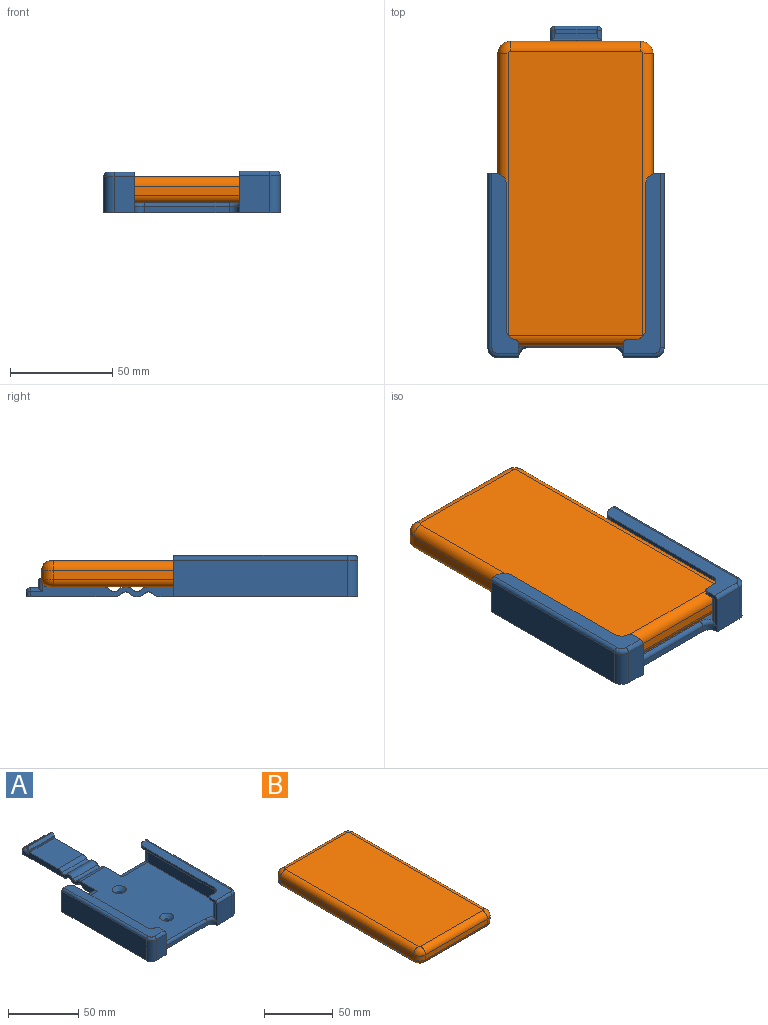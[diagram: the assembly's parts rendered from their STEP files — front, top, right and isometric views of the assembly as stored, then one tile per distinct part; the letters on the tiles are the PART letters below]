
ASSEMBLY  parts=2 mates=1
PART A: 85 faces, bbox 87.1x162.5x20.6 mm
  f0: plane 98.24x76.2mm, normal (0,0,1), area 6276mm2, adj f10,f11,f14,f16,f38,f39,f41,f42
  f1: plane 96.64x86.2mm, normal (0,0,-1), area 7642.9mm2, adj f6,f9,f13,f15,f18,f28,f29,f30
  f2: plane 4x2mm, normal (0,1,0), area 7.1mm2, adj f19,f20,f37,f84
  f3: plane 71x2mm, normal (-1,0,0), area 142mm2, adj f23,f24,f27,f83
  f4: plane 71.07x2mm, normal (1,0,0), area 142.1mm2, adj f19,f20,f22,f84
  f5: plane 4x2mm, normal (0,1,0), area 7.1mm2, adj f23,f24,f34,f83
  f6: plane 41.2x3mm, normal (0,-1,0), area 123.6mm2, adj f1,f28,f29,f48
  f7: plane 28.41x25mm, normal (0,0,1), area 710.2mm2, adj f38,f39,f44,f70
  f8: plane 43x25mm, normal (0,0,-1), area 1073.3mm2, adj f38,f39,f51,f69,f75,f78
  f9: plane 85x18.5mm, normal (1,0,0), area 1572.5mm2, adj f1,f31,f34,f43
  f10: plane 80x13.5mm, normal (-1,0,0), area 1080mm2, adj f0,f11,f23,f43
  f11: plane 13.5x12mm, normal (0,1,0), area 162mm2, adj f0,f10,f23,f72
  f12: plane 17.55x7.05mm, normal (-1,0,0), area 42.9mm2, adj f13,f23,f24,f26,f32,f49,f72
  f13: plane 18.5x15mm, normal (0,-1,0), area 277.5mm2, adj f1,f12,f29,f31,f32
  f14: plane 80x13mm, normal (1,0,0), area 1040mm2, adj f0,f16,f20,f40
  f15: plane 85x18mm, normal (-1,0,0), area 1530mm2, adj f1,f30,f37,f40
  f16: plane 13x7mm, normal (0,1,0), area 91mm2, adj f0,f14,f20,f71
  f17: plane 17.05x7.05mm, normal (1,0,0), area 41.9mm2, adj f18,f19,f20,f21,f35,f47,f71
  f18: plane 18x10mm, normal (0,-1,0), area 180mm2, adj f1,f17,f28,f30,f35
  f19: plane 88x13mm, normal (0,0,1), area 654.9mm2, adj f2,f4,f17,f21,f22,f35,f36,f37
  f20: plane 88x15mm, normal (0,0,-1), area 370.1mm2, adj f2,f4,f14,f16,f17,f21,f22,f40
  f21: cylinder r=2mm len=2mm, axis (0,0,-1), area 5.7mm2, adj f17,f19,f20,f22
  f22: cylinder r=5mm len=4.95mm, axis (0,0,-1), area 14.3mm2, adj f4,f19,f20,f21
  f23: plane 88x20mm, normal (0,0,-1), area 390.4mm2, adj f3,f5,f10,f11,f12,f25,f26,f27
  f24: plane 88x18mm, normal (0,0,1), area 690.2mm2, adj f3,f5,f12,f25,f26,f27,f32,f33
  f25: plane 4x2mm, normal (0,1,0), area 8mm2, adj f23,f24,f26,f27
  f26: cylinder r=2mm len=2mm, axis (0,0,1), area 6.3mm2, adj f12,f23,f24,f25
  f27: cylinder r=5mm len=5mm, axis (0,0,-1), area 15.7mm2, adj f3,f23,f24,f25
  f28: cylinder r=5mm len=5mm, axis (0,0,1), area 23.6mm2, adj f1,f6,f18,f47
  f29: cylinder r=5mm len=5mm, axis (0,0,-1), area 23.6mm2, adj f1,f6,f13,f49
  f30: cylinder r=5mm len=18mm, axis (0,0,-1), area 141.4mm2, adj f1,f15,f18,f36
  f31: cylinder r=5mm len=18.5mm, axis (0,0,-1), area 145.3mm2, adj f1,f9,f13,f33
  f32: cylinder r=2mm len=15mm, axis (-1,0,0), area 47.1mm2, adj f12,f13,f24,f33
  f33: torus R=3mm, axis (0,0,1), area 21.1mm2, adj f24,f31,f32,f34
  f34: cylinder r=2mm len=85mm, axis (0,-1,0), area 267mm2, adj f5,f9,f24,f33
  f35: cylinder r=2mm len=10mm, axis (1,0,0), area 31.4mm2, adj f17,f18,f19,f36
  f36: torus R=3mm, axis (0,0,1), area 21.1mm2, adj f19,f30,f35,f37
  f37: cylinder r=2mm len=85mm, axis (0,-1,0), area 267mm2, adj f2,f15,f19,f36
  f38: plane 75x8mm, normal (1,0,0), area 294.1mm2, adj f0,f1,f7,f8,f42,f44,f46,f61
  f39: plane 75x8mm, normal (-1,0,0), area 294.1mm2, adj f0,f1,f7,f8,f41,f44,f46,f61
  f40: cylinder r=5mm len=18mm, axis (0,0,-1), area 116.4mm2, adj f14,f15,f20,f41
  f41: cylinder r=5mm len=30.6mm, axis (1,0,0), area 215.3mm2, adj f0,f1,f39,f40
  f42: cylinder r=5mm len=30.6mm, axis (1,0,0), area 215.3mm2, adj f0,f1,f38,f43
  f43: cylinder r=5mm len=18.5mm, axis (0,0,-1), area 120.3mm2, adj f9,f10,f23,f42
  f44: plane 25x2mm, normal (0,-1,0), area 50mm2, adj f7,f38,f39,f46
  f45: plane 21x3.5mm, normal (0,1,0), area 73.5mm2, adj f50,f73,f74,f82
  f46: plane 25.04x2.04mm, normal (0,-0.71,0.71), area 70.5mm2, adj f38,f39,f44,f73,f74,f82
  f47: torus R=7mm, axis (0,0,1), area 20.9mm2, adj f0,f17,f28,f48,f71
  f48: cylinder r=2mm len=41.2mm, axis (-1,0,0), area 129.4mm2, adj f0,f6,f47,f49
  f49: torus R=7mm, axis (0,0,1), area 20.9mm2, adj f0,f12,f29,f48,f72
  f50: plane 21x4mm, normal (0,0,1), area 48.4mm2, adj f45,f52,f53,f54,f76,f79,f81
  f51: plane 21x2.5mm, normal (0,1,0), area 52.5mm2, adj f8,f75,f78,f79
  f52: plane 2x0.7mm, normal (1,0,0), area 1.4mm2, adj f50,f53,f55,f56,f79
  f53: plane 20x0.7mm, normal (0,1,0), area 14mm2, adj f50,f52,f54,f56
  f54: plane 2x0.7mm, normal (-1,0,0), area 1.4mm2, adj f50,f53,f55,f56,f79
  f55: plane 20x0.69mm, normal (0,-1,0), area 13.8mm2, adj f52,f54,f56,f79
  f56: plane 20x2mm, normal (0,0,1), area 40mm2, adj f52,f53,f54,f55
  f57: cylinder r=2mm len=4mm, axis (0,0,1), area 25.1mm2, adj f1,f58
  f58: cone r=2mm half-angle=45deg, axis (0,0,1), area 93.3mm2, adj f0,f57
  f59: cylinder r=2mm len=4mm, axis (0,0,1), area 25.1mm2, adj f1,f60
  f60: cone r=2mm half-angle=45deg, axis (0,0,1), area 93.3mm2, adj f0,f59
  f61: cylinder r=2.5mm len=25mm, axis (1,0,0), area 105.1mm2, adj f38,f39,f66,f69
  f62: cylinder r=2.5mm len=25mm, axis (1,0,0), area 105.1mm2, adj f38,f39,f65,f66
  f63: cylinder r=2.5mm len=25mm, axis (1,0,0), area 105.1mm2, adj f38,f39,f68,f70
  f64: cylinder r=2.5mm len=25mm, axis (1,0,0), area 105.1mm2, adj f38,f39,f67,f68
  f65: cylinder r=5mm len=25mm, axis (1,0,0), area 105.1mm2, adj f1,f38,f39,f62
  f66: cylinder r=5mm len=25mm, axis (1,0,0), area 210.3mm2, adj f38,f39,f61,f62
  f67: cylinder r=5mm len=25mm, axis (1,0,0), area 105.1mm2, adj f0,f38,f39,f64
  f68: cylinder r=5mm len=25mm, axis (1,0,0), area 210.3mm2, adj f38,f39,f63,f64
  f69: cylinder r=5mm len=25mm, axis (1,0,0), area 105.1mm2, adj f8,f38,f39,f61
  f70: cylinder r=5mm len=25mm, axis (1,0,0), area 105.1mm2, adj f7,f38,f39,f63
  f71: cylinder r=3mm len=13.82mm, axis (0,0,1), area 61.9mm2, adj f0,f16,f17,f20,f47
  f72: cylinder r=3mm len=14.32mm, axis (0,0,-1), area 64.3mm2, adj f0,f11,f12,f23,f49
  f73: cylinder r=1mm len=24.46mm, axis (-1,0,0), area 36.1mm2, adj f45,f46,f74,f82
  f74: cylinder r=2mm len=6.5mm, axis (0,0,-1), area 15.1mm2, adj f38,f45,f46,f73,f76
  f75: cylinder r=2mm len=2.5mm, axis (0,0,-1), area 7.9mm2, adj f8,f38,f51,f77
  f76: cylinder r=2mm len=6mm, axis (0,1,0), area 14.8mm2, adj f38,f50,f74,f77
  f77: sphere r=2mm, area 6.3mm2, adj f75,f76,f79
  f78: cylinder r=2mm len=2.5mm, axis (0,0,1), area 7.9mm2, adj f8,f39,f51,f80
  f79: cylinder r=2mm len=21mm, axis (-1,0,0), area 61.5mm2, adj f50,f51,f52,f54,f55,f77,f80
  f80: sphere r=2mm, area 6.3mm2, adj f78,f79,f81
  f81: cylinder r=2mm len=6mm, axis (0,-1,0), area 14.8mm2, adj f39,f50,f80,f82
  f82: cylinder r=2mm len=6.5mm, axis (0,0,1), area 15.1mm2, adj f39,f45,f46,f73,f81
  f83: cylinder r=5mm len=5mm, axis (0,0,-1), area 15.7mm2, adj f3,f5,f23,f24
  f84: cylinder r=5mm len=5mm, axis (0,0,1), area 15.7mm2, adj f2,f4,f19,f20
PART B: 26 faces, bbox 75.8x148.9x12.8 mm
  f0: plane 63.8x4.3mm, normal (0,-1,0), area 274.3mm2, adj f6,f9,f17,f25
  f1: plane 136.86x4.3mm, normal (1,0,0), area 588.5mm2, adj f6,f7,f13,f21
  f2: plane 63.8x4.3mm, normal (0,1,0), area 274.3mm2, adj f7,f8,f10,f18
  f3: plane 136.86x4.3mm, normal (-1,0,0), area 588.5mm2, adj f8,f9,f14,f22
  f4: plane 138.86x65.8mm, normal (0,0,1), area 9136.1mm2, adj f18,f19,f20,f21,f22,f23,f24,f25
  f5: plane 141.86x68.8mm, normal (0,0,-1), area 9754.6mm2, adj f10,f11,f12,f13,f14,f15,f16,f17
  f6: cylinder r=6mm len=6mm, axis (0,0,-1), area 40.5mm2, adj f0,f1,f15,f23
  f7: cylinder r=6mm len=6mm, axis (0,0,1), area 40.5mm2, adj f1,f2,f11,f19
  f8: cylinder r=6mm len=6mm, axis (0,0,-1), area 40.5mm2, adj f2,f3,f12,f20
  f9: cylinder r=6mm len=6mm, axis (0,0,1), area 40.5mm2, adj f0,f3,f16,f24
  f10: cylinder r=3.5mm len=63.8mm, axis (-1,0,0), area 350.8mm2, adj f2,f5,f11,f12
  f11: torus R=2.5mm, axis (0,0,1), area 40.8mm2, adj f5,f7,f10,f13
  f12: torus R=2.5mm, axis (0,0,1), area 40.8mm2, adj f5,f8,f10,f14
  f13: cylinder r=3.5mm len=136.86mm, axis (0,1,0), area 752.4mm2, adj f1,f5,f11,f15
  f14: cylinder r=3.5mm len=136.86mm, axis (0,-1,0), area 752.4mm2, adj f3,f5,f12,f16
  f15: torus R=2.5mm, axis (0,0,1), area 40.8mm2, adj f5,f6,f13,f17
  f16: torus R=2.5mm, axis (0,0,1), area 40.8mm2, adj f5,f9,f14,f17
  f17: cylinder r=3.5mm len=63.8mm, axis (1,0,0), area 350.8mm2, adj f0,f5,f15,f16
  f18: cylinder r=5mm len=63.8mm, axis (1,0,0), area 501.1mm2, adj f2,f4,f19,f20
  f19: torus R=1mm, axis (0,0,1), area 51.6mm2, adj f4,f7,f18,f21
  f20: torus R=1mm, axis (0,0,1), area 51.6mm2, adj f4,f8,f18,f22
  f21: cylinder r=5mm len=136.86mm, axis (0,-1,0), area 1074.9mm2, adj f1,f4,f19,f23
  f22: cylinder r=5mm len=136.86mm, axis (0,1,0), area 1074.9mm2, adj f3,f4,f20,f24
  f23: torus R=1mm, axis (0,0,1), area 51.6mm2, adj f4,f6,f21,f25
  f24: torus R=1mm, axis (0,0,1), area 51.6mm2, adj f4,f9,f22,f25
  f25: cylinder r=5mm len=63.8mm, axis (-1,0,0), area 501.1mm2, adj f0,f4,f23,f24
PLACE A rot(axis=(0.4,-0.66,0.64),0deg) t=(88.83,17.37,85.67)mm
PLACE B rot(axis=(0.4,-0.66,0.64),0deg) t=(88.58,50.02,90.67)mm
MATE planar A.f0 <-> B.f5  axis (0,0,1) through (88.87,18.63,90.67)mm
